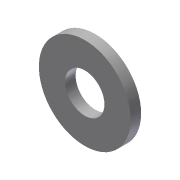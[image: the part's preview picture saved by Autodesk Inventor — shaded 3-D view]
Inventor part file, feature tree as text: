
AUTODESK INVENTOR PART (.ipt)
format: ipt  version: 2015 (Build 190159000, 159)  size: 77,824 bytes
history: native  units: in
note: dims shown in document units (in); Inventor stores cm internally (conversion verified against a paired STEP export)
features: extrude x1, sketch x1
ambient origin geometry x8: Origin, YZ Plane, XZ Plane, XY Plane, X Axis, Y Axis, Z Axis, Center Point
bodies: Solid1 (feature_tree)
feature tree (2):
  extrude  "Extrusion1"  Depth=0.05in
  sketch  "Sketch1"  dims[d0=0.1875in d1=0.4375in d2=0.05in d3=0.0in]
